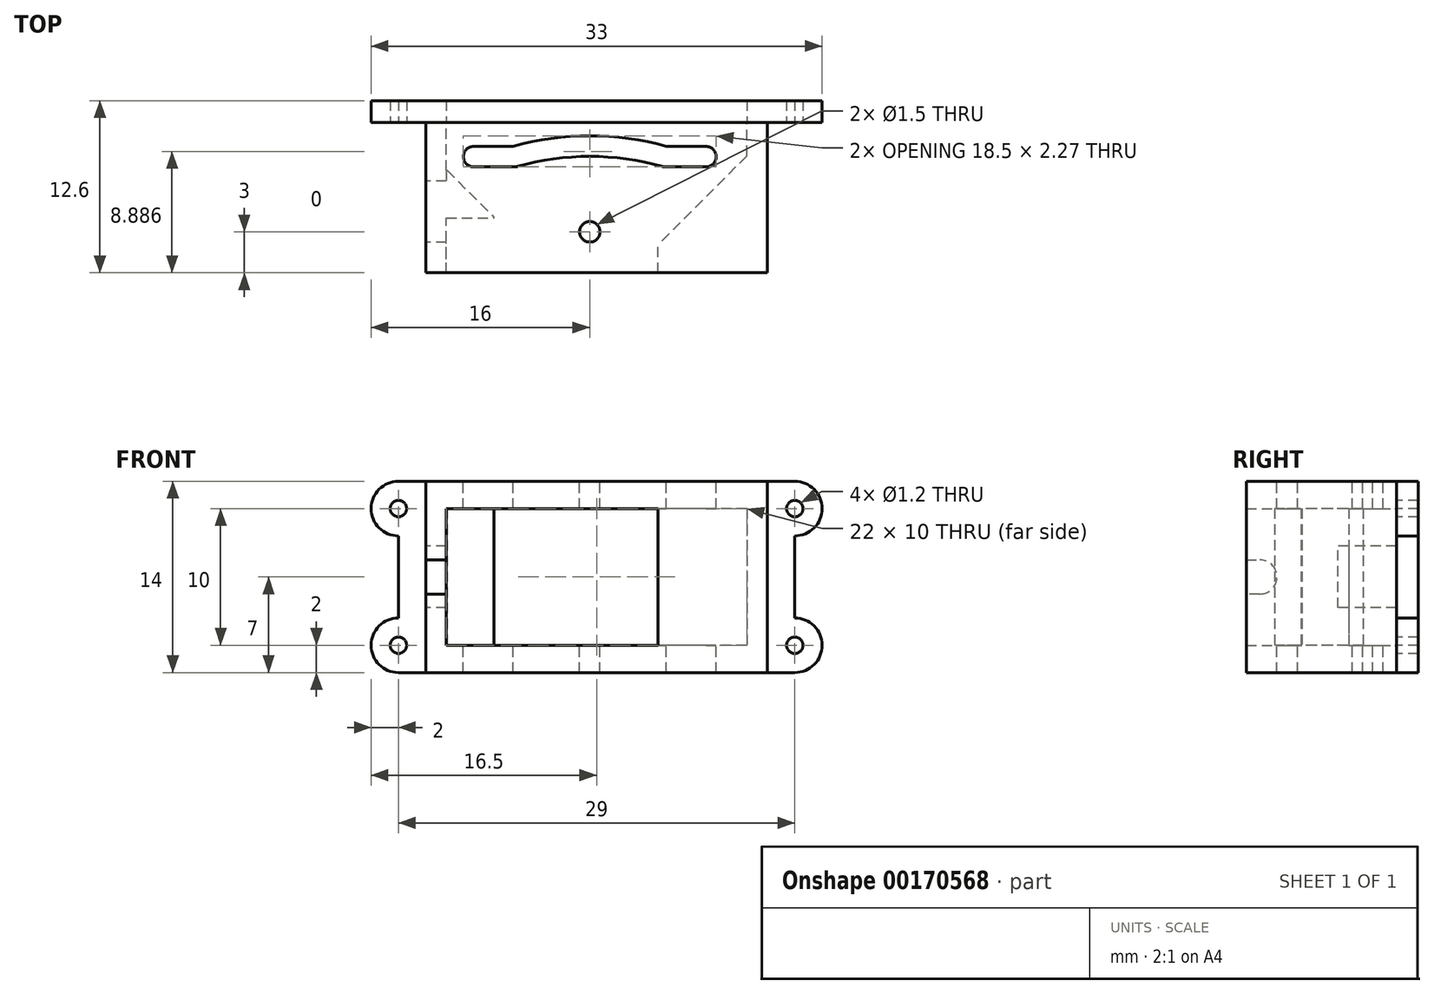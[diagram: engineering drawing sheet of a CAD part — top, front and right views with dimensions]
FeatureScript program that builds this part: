
annotation { "Feature Type Name" : "Feature", "Feature Type Description" : "" }
export const myFeature = defineFeature(function(context is Context, id is Id, definition is map)
    precondition{}
    {
        {
            var Q0;
            Q0=qCreatedBy(makeId("Front.planeOp"),FACE);
            var sketch = newSketch(context, id + "F0", { "sketchPlane" : qUnion([Q0])});
            skLineSegment(sketch, "E0.bottom", {"start": v(12.5, 7) * mm, "end": v(-12.5, 7) * mm});
            skLineSegment(sketch, "E0.top", {"start": v(12.5, -7) * mm, "end": v(-12.5, -7) * mm});
            skLineSegment(sketch, "E0.left", {"start": v(12.5, 7) * mm, "end": v(12.5, -7) * mm});
            skLineSegment(sketch, "E0.right", {"start": v(-12.5, 7) * mm, "end": v(-12.5, -7) * mm});
            skPoint(sketch, "E0.middle", {"position": v(0, 0) * mm});
            skLineSegment(sketch, "E1.bottom", {"start": v(11, 5) * mm, "end": v(-11, 5) * mm});
            skLineSegment(sketch, "E1.top", {"start": v(11, -5) * mm, "end": v(-11, -5) * mm});
            skLineSegment(sketch, "E1.left", {"start": v(11, 5) * mm, "end": v(11, -5) * mm});
            skLineSegment(sketch, "E1.right", {"start": v(-11, 5) * mm, "end": v(-11, -5) * mm});
            skSolve(sketch);
        }
        {
            var Q0;
            Q0=makeQuery(id+"F0.imprint","IMPRINT",FACE,{"disambiguationData":[TD([[makeQuery(id+"F0.imprint","IMPRINT",EDGE,{"derivedFrom":sQuery(id+"F0.wireOp",EDGE,"E0.bottom")}),1.0]])]});
            extrude(context, id + "F1", {"entities" : qUnion([Q0]), "depth" : 11 * mm});
        }
        {
            var Q0;
            Q0=qCreatedBy(makeId("Top.planeOp"),FACE);
            var sketch = newSketch(context, id + "F2", { "sketchPlane" : qUnion([Q0])});
            skCircle(sketch, "E2", {"center": v(-0.5, -8) * mm, "radius": 0.75 * mm});
            skLineSegment(sketch, "E3", {"start": v(-0.5, -8) * mm, "end": v(-0.5, -21.73) * mm, "construction": true});
            skArc(sketch, "E4", {"start": v(-6, -2.5) * mm, "mid": v(-3.28, -1.92) * mm, "end": v(-0.5, -1.73) * mm});
            skLineSegment(sketch, "E5", {"start": v(-0.5, -8) * mm, "end": v(-0.5, -1.73) * mm, "construction": true});
            skLineSegment(sketch, "E6", {"start": v(-0.5, -8) * mm, "end": v(-6, -2.5) * mm, "construction": true});
            skLineSegment(sketch, "E7", {"start": v(-6, -2.5) * mm, "end": v(-9, -2.5) * mm});
            skLineSegment(sketch, "E8.MirrorCS", {"start": v(5, -2.5) * mm, "end": v(8, -2.5) * mm});
            skArc(sketch, "E9.MirrorCS", {"start": v(5, -2.5) * mm, "mid": v(2.28, -1.92) * mm, "end": v(-0.5, -1.73) * mm});
            skArc(sketch, "E10.0.startCap", {"start": v(-5.8, -3.22) * mm, "mid": v(-6.72, -2.7) * mm, "end": v(-6.2, -1.78) * mm});
            skArc(sketch, "E10.0.endCap", {"start": v(-0.5, -0.98) * mm, "mid": v(0.25, -1.73) * mm, "end": v(-0.5, -2.48) * mm});
            skArc(sketch, "E10.0.left", {"start": v(-6.2, -1.78) * mm, "mid": v(-3.38, -1.18) * mm, "end": v(-0.5, -0.98) * mm});
            skArc(sketch, "E10.0.right", {"start": v(-5.8, -3.22) * mm, "mid": v(-3.17, -2.67) * mm, "end": v(-0.5, -2.48) * mm});
            skArc(sketch, "E10.1.startCap", {"start": v(5.2, -1.78) * mm, "mid": v(5.72, -2.7) * mm, "end": v(4.8, -3.22) * mm});
            skArc(sketch, "E10.1.endCap", {"start": v(-0.5, -2.48) * mm, "mid": v(-1.25, -1.73) * mm, "end": v(-0.5, -0.98) * mm});
            skArc(sketch, "E10.1.left", {"start": v(4.8, -3.22) * mm, "mid": v(2.17, -2.67) * mm, "end": v(-0.5, -2.48) * mm});
            skArc(sketch, "E10.1.right", {"start": v(5.2, -1.78) * mm, "mid": v(2.38, -1.18) * mm, "end": v(-0.5, -0.98) * mm});
            skArc(sketch, "E10.2.startCap", {"start": v(5, -3.25) * mm, "mid": v(4.25, -2.5) * mm, "end": v(5, -1.75) * mm});
            skArc(sketch, "E10.2.endCap", {"start": v(8, -1.75) * mm, "mid": v(8.75, -2.5) * mm, "end": v(8, -3.25) * mm});
            skLineSegment(sketch, "E10.2.left", {"start": v(5, -1.75) * mm, "end": v(8, -1.75) * mm});
            skLineSegment(sketch, "E10.2.right", {"start": v(5, -3.25) * mm, "end": v(8, -3.25) * mm});
            skArc(sketch, "E10.3.startCap", {"start": v(-6, -1.75) * mm, "mid": v(-5.25, -2.5) * mm, "end": v(-6, -3.25) * mm});
            skArc(sketch, "E10.3.endCap", {"start": v(-9, -3.25) * mm, "mid": v(-9.75, -2.5) * mm, "end": v(-9, -1.75) * mm});
            skLineSegment(sketch, "E10.3.left", {"start": v(-6, -3.25) * mm, "end": v(-9, -3.25) * mm});
            skLineSegment(sketch, "E10.3.right", {"start": v(-6, -1.75) * mm, "end": v(-9, -1.75) * mm});
            skSolve(sketch);
        }
        {
            var Q0;
            Q0 = qSketchRegion(id + "F2", true);
            extrude(context, id + "F3", {"entities" : qUnion([Q0]), "operationType" : NewBodyOperationType.REMOVE, "endBound" : BoundingType.SYMMETRIC, "oppositeDirection" : true, "depth" : 25 * mm});
        }
        {
            var Q0;
            Q0=makeQuery(id+"F1.opExtrude","SWEPT_FACE",FACE,{"disambiguationData":[OSD([sQuery(id+"F0.wireOp",EDGE,"E0.right")])]});
            var sketch = newSketch(context, id + "F4", { "sketchPlane" : qUnion([Q0])});
            skLineSegment(sketch, "E11.bottom", {"start": v(0, -2.25) * mm, "end": v(4.3, -2.25) * mm});
            skLineSegment(sketch, "E11.top", {"start": v(0, 2.25) * mm, "end": v(4.3, 2.25) * mm});
            skLineSegment(sketch, "E11.left", {"start": v(0, -2.25) * mm, "end": v(0, 2.25) * mm});
            skLineSegment(sketch, "E11.right", {"start": v(4.3, -2.25) * mm, "end": v(4.3, 2.25) * mm});
            skLineSegment(sketch, "E12", {"start": v(4.3, 0) * mm, "end": v(11, 0) * mm, "construction": true});
            skArc(sketch, "E13", {"start": v(10, 1.25) * mm, "mid": v(8.75, 0) * mm, "end": v(10, -1.25) * mm});
            skLineSegment(sketch, "E14", {"start": v(10, -1.25) * mm, "end": v(11, -1.25) * mm});
            skLineSegment(sketch, "E15", {"start": v(11, -1.25) * mm, "end": v(11, 1.25) * mm});
            skLineSegment(sketch, "E16", {"start": v(11, 1.25) * mm, "end": v(10, 1.25) * mm});
            skSolve(sketch);
        }
        {
            var Q0;
            Q0 = qSketchRegion(id + "F4", true);
            extrude(context, id + "F5", {"entities" : qUnion([Q0]), "operationType" : NewBodyOperationType.REMOVE, "endBound" : BoundingType.UP_TO_NEXT, "oppositeDirection" : true, "depth" : 16.29 * mm});
        }
        {
            var Q0;
            Q0=qCreatedBy(makeId("Top.planeOp"),FACE);
            var sketch = newSketch(context, id + "F6", { "sketchPlane" : qUnion([Q0])});
            skLineSegment(sketch, "E17.0", {"start": v(-0.5, -8) * mm, "end": v(-6, -2.5) * mm, "construction": true});
            skLineSegment(sketch, "E17.1", {"start": v(-0.5, -8) * mm, "end": v(-0.5, -1.73) * mm, "construction": true});
            skLineSegment(sketch, "E17.2", {"start": v(-0.5, -8) * mm, "end": v(-0.5, -21.73) * mm, "construction": true});
            skLineSegment(sketch, "E18.MirrorCS", {"start": v(-0.5, -8) * mm, "end": v(5, -2.5) * mm, "construction": true});
            skLineSegment(sketch, "E19", {"start": v(4.5, -8.94) * mm, "end": v(11, -2.44) * mm});
            skLineSegment(sketch, "E20", {"start": v(-7.5, -6.94) * mm, "end": v(-10.94, -3.5) * mm});
            skLineSegment(sketch, "E21.0", {"start": v(11, -11) * mm, "end": v(-0.5, -11) * mm});
            skLineSegment(sketch, "E22", {"start": v(4.5, -8.94) * mm, "end": v(4.5, -11) * mm});
            skLineSegment(sketch, "E23.0", {"start": v(11, -11) * mm, "end": v(11, -2.44) * mm});
            skPoint(sketch, "E24.orphan", {"position": v(11, 0) * mm});
            skPoint(sketch, "E25.0.end.orphan", {"position": v(12.5, 0) * mm});
            skPoint(sketch, "E26.orphan", {"position": v(12.5, -11) * mm});
            skLineSegment(sketch, "E27", {"start": v(-7.5, -6.94) * mm, "end": v(-7.5, -7) * mm});
            skLineSegment(sketch, "E28.0", {"start": v(-11, -7) * mm, "end": v(-11, -3.5) * mm});
            skLineSegment(sketch, "E29", {"start": v(-10.94, -3.5) * mm, "end": v(-11, -3.5) * mm});
            skLineSegment(sketch, "E30", {"start": v(-7.5, -7) * mm, "end": v(-11, -7) * mm});
            skPoint(sketch, "E31.orphan", {"position": v(-11, 0) * mm});
            skSolve(sketch);
        }
        {
            var Q0;
            Q0 = qSketchRegion(id + "F6", true);
            extrude(context, id + "F7", {"entities" : qUnion([Q0]), "operationType" : NewBodyOperationType.ADD, "endBound" : BoundingType.UP_TO_NEXT, "depth" : 25 * mm, "hasSecondDirection" : true, "secondDirectionBound" : SecondDirectionBoundingType.UP_TO_NEXT, "secondDirectionOppositeDirection" : true, "secondDirectionDepth" : 25 * mm});
        }
        {
            var Q0;
            Q0=makeQuery(id+"F1.opExtrude","CAP_FACE",FACE,{"disambiguationData":[OSD([sQuery(id+"F0.wireOp",EDGE,"E0.bottom"),sQuery(id+"F0.wireOp",EDGE,"E0.top"),sQuery(id+"F0.wireOp",EDGE,"E0.left"),sQuery(id+"F0.wireOp",EDGE,"E0.right"),sQuery(id+"F0.wireOp",EDGE,"E1.bottom"),sQuery(id+"F0.wireOp",EDGE,"E1.top"),sQuery(id+"F0.wireOp",EDGE,"E1.left"),sQuery(id+"F0.wireOp",EDGE,"E1.right")])],"isStart":true});
            var sketch = newSketch(context, id + "F8", { "sketchPlane" : qUnion([Q0])});
            skLineSegment(sketch, "E32.0", {"start": v(-11, -5) * mm, "end": v(11, -5) * mm});
            skLineSegment(sketch, "E33.0", {"start": v(-11, 5) * mm, "end": v(11, 5) * mm});
            skLineSegment(sketch, "E34.0", {"start": v(-11, 5) * mm, "end": v(-11, -5) * mm});
            skLineSegment(sketch, "E35", {"start": v(11, 5) * mm, "end": v(11, -5) * mm});
            skLineSegment(sketch, "E36.0", {"start": v(-12.5, -7) * mm, "end": v(12.5, -7) * mm});
            skLineSegment(sketch, "E37", {"start": v(-12.5, 0) * mm, "end": v(4.19, 0) * mm, "construction": true});
            skPoint(sketch, "E37.endSnap0", {"position": v(-12.5, 0) * mm});
            skCircle(sketch, "E38", {"center": v(-14.5, -5) * mm, "radius": 0.6 * mm});
            skLineSegment(sketch, "E39", {"start": v(0, -7) * mm, "end": v(0, 7) * mm, "construction": true});
            skLineSegment(sketch, "E40", {"start": v(-12.5, -7) * mm, "end": v(-14.5, -7) * mm});
            skArc(sketch, "E41", {"start": v(-14.5, -7) * mm, "mid": v(-16.5, -5) * mm, "end": v(-14.5, -3) * mm});
            skLineSegment(sketch, "E42", {"start": v(-14.5, -3) * mm, "end": v(-14.5, 0) * mm});
            skArc(sketch, "E43.MirrorCS", {"start": v(-14.5, 7) * mm, "mid": v(-16.5, 5) * mm, "end": v(-14.5, 3) * mm});
            skLineSegment(sketch, "E44.MirrorCS", {"start": v(-14.5, 3) * mm, "end": v(-14.5, 0) * mm});
            skCircle(sketch, "E45.MirrorC", {"center": v(-14.5, 5) * mm, "radius": 0.6 * mm});
            skLineSegment(sketch, "E46.MirrorCS", {"start": v(-12.5, 7) * mm, "end": v(-14.5, 7) * mm});
            skPoint(sketch, "E47.MirrorP", {"position": v(12.5, 0) * mm});
            skArc(sketch, "E48.MirrorCS", {"start": v(14.5, -7) * mm, "mid": v(16.5, -5) * mm, "end": v(14.5, -3) * mm});
            skLineSegment(sketch, "E49.MirrorCS", {"start": v(12.5, -7) * mm, "end": v(14.5, -7) * mm});
            skCircle(sketch, "E50.MirrorC", {"center": v(14.5, -5) * mm, "radius": 0.6 * mm});
            skLineSegment(sketch, "E51.MirrorCS", {"start": v(14.5, -3) * mm, "end": v(14.5, 0) * mm});
            skLineSegment(sketch, "E52.MirrorCS", {"start": v(14.5, 3) * mm, "end": v(14.5, 0) * mm});
            skArc(sketch, "E53.MirrorCS", {"start": v(14.5, 7) * mm, "mid": v(16.5, 5) * mm, "end": v(14.5, 3) * mm});
            skCircle(sketch, "E54.MirrorC", {"center": v(14.5, 5) * mm, "radius": 0.6 * mm});
            skLineSegment(sketch, "E55.MirrorCS", {"start": v(12.5, 7) * mm, "end": v(14.5, 7) * mm});
            skSolve(sketch);
        }
        {
            var Q0;
            Q0=makeQuery(id+"F8.imprint","IMPRINT",FACE,{"disambiguationData":[TD([[makeQuery(id+"F8.imprint","IMPRINT",EDGE,{"derivedFrom":sQuery(id+"F8.wireOp",EDGE,"E48.MirrorCS")}),1.0]])]});
            var Q1;
            {var subQ6=sQuery(id+"F8.wireOp",EDGE,"E32.0");Q1=makeQuery(id+"F8.imprint","IMPRINT",FACE,{"disambiguationData":[TD([[makeQuery(id+"F8.imprint","IMPRINT",EDGE,{"derivedFrom":subQ6}),-1.0]])]});}
            var Q2;
            Q2=makeQuery(id+"F8.imprint","IMPRINT",FACE,{"disambiguationData":[TD([[makeQuery(id+"F8.imprint","IMPRINT",EDGE,{"derivedFrom":sQuery(id+"F8.wireOp",EDGE,"E38")}),-1.0]])]});
            extrude(context, id + "F9", {"entities" : qUnion([Q0, Q1, Q2]), "depth" : 1.6 * mm});
        }
    });
